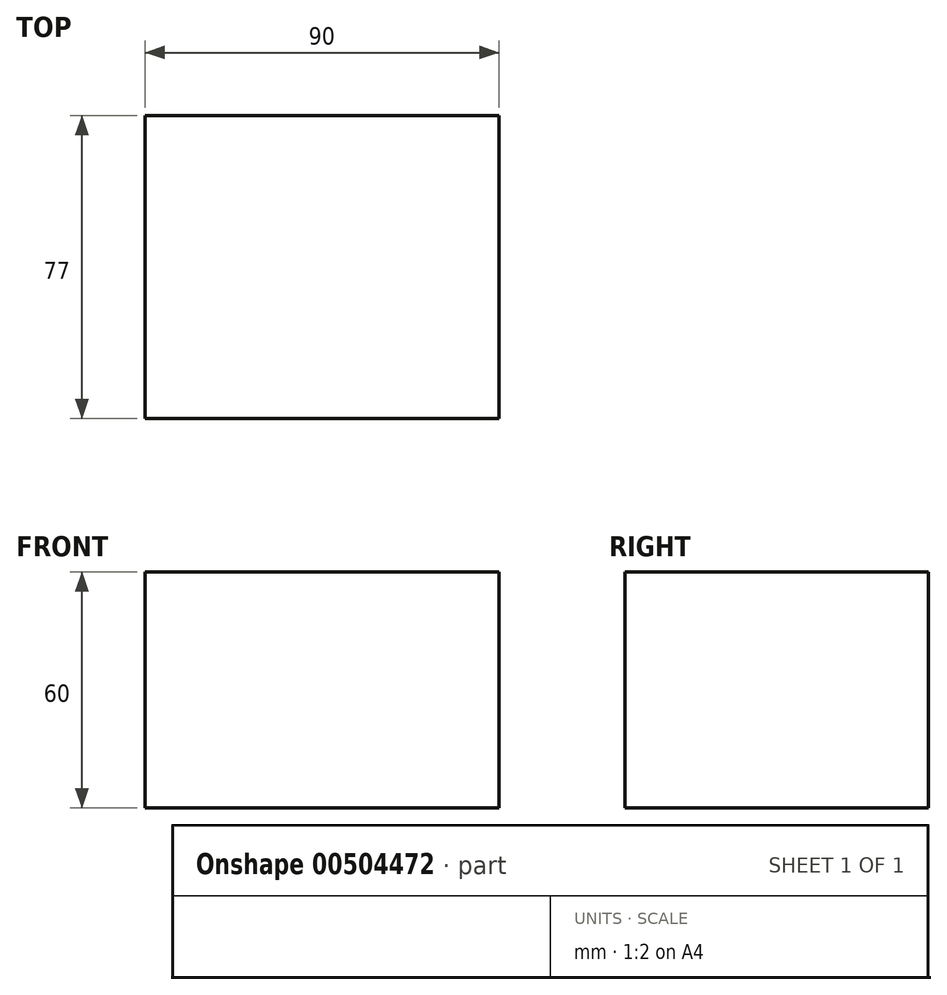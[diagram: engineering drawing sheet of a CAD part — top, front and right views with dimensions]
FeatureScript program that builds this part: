
annotation { "Feature Type Name" : "Feature", "Feature Type Description" : "" }
export const myFeature = defineFeature(function(context is Context, id is Id, definition is map)
    precondition{}
    {
        {
            var Q0;
            Q0=qCreatedBy(makeId("Front.planeOp"),FACE);
            var sketch = newSketch(context, id + "F0", { "sketchPlane" : qUnion([Q0])});
            skLineSegment(sketch, "E0.bottom", {"start": v(-45, 60) * mm, "end": v(45, 60) * mm});
            skLineSegment(sketch, "E0.top", {"start": v(-45, 0) * mm, "end": v(45, 0) * mm});
            skLineSegment(sketch, "E0.left", {"start": v(-45, 60) * mm, "end": v(-45, 0) * mm});
            skLineSegment(sketch, "E0.right", {"start": v(45, 60) * mm, "end": v(45, 0) * mm});
            skSolve(sketch);
        }
        {
            var Q0;
            Q0 = qSketchRegion(id + "F0", true);
            extrude(context, id + "F1", {"entities" : qUnion([Q0]), "depth" : (77 / 2) * mm, "offsetDistance" : 25 * mm, "hasSecondDirection" : true, "secondDirectionOppositeDirection" : true, "secondDirectionDepth" : (77 / 2) * mm});
        }
    });
